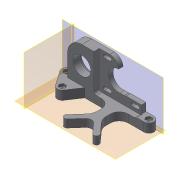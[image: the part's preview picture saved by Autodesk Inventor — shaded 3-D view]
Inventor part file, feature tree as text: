
AUTODESK INVENTOR PART (.ipt)
format: ipt  version: 2015 SP2 (Build 190223200, 223)  size: 351,744 bytes
history: native  units: mm
features: extrude x10, sketch x10, projected_geometry x4, chamfer x2, fillet x2, pattern_linear x2, other x1
ambient origin geometry x8: Origin, YZ Plane, XZ Plane, XY Plane, X Axis, Y Axis, Z Axis, Center Point
bodies: Body1 (feature_tree)
feature tree (31):
  other  "Sólido1"
  extrude  "Extrusión1"  Depth=5.5mm
  extrude  "Extrusión2"  Depth=5.0mm
  extrude  "Extrusión3"  Depth=10.0mm
  extrude  "Extrusión4"  Depth=3.0mm
  extrude  "Extrusión5"  Depth=6.0mm
  chamfer  "Chaflán2"  Distance=91.459mm
  chamfer  "Chaflán3"  Distance=5.5mm
  extrude  "Extrusión6"  Depth=11.967723mm
  extrude  "Extrusión7"  Depth=10.0mm
  extrude  "Extrusión8"  Depth=10.0mm
  fillet  "Empalme2"  Radius=3.76mm
  extrude  "Extrusión10"  Depth=10.0mm TaperAngle=0.0deg
  pattern_linear  "Patrón rectangular1"  Spacing1=6.235mm  [1 undecoded]
  pattern_linear  "Patrón rectangular2"  Spacing1=6.235mm  [1 undecoded]
  fillet  "Empalme3"  Radius=6.235mm
  extrude  "Extrusión11"  Depth=2.79mm TaperAngle=0.0deg
  sketch  "Boceto2"  dims[d19=91.459mm d20=5.5mm]
  sketch  "Boceto4"  dims[d21=5.0mm d22=5.0mm]
  sketch  "Boceto5"  dims[d25=10.0mm d28=14.666002mm]
  projected_geometry  "Contorno proyectado1"
  sketch  "Boceto6"  dims[d29=15.75mm d31=3.0mm]
  sketch  "Boceto7"  dims[d32=3.0mm d34=6.0mm]
  sketch  "Boceto8"  dims[d35=3.76mm]
  projected_geometry  "Contorno proyectado2"
  sketch  "Boceto9"  dims[d36=3.76mm]
  sketch  "Boceto10"  dims[d37=10.0mm]
  projected_geometry  "Contorno proyectado3"
  sketch  "Boceto12"  dims[d38=5.5mm]
  projected_geometry  "Contorno proyectado4"
  sketch  "Boceto13"  dims[d39=5.5mm d40=91.459mm d41=5.5mm d42=11.967723mm d43=21.587978mm d44=20.112mm d46=3.76mm d47=10.0mm d48=0.0mm d49=6.235mm d50=6.235mm d51=6.235mm d52=2.79mm d53=0.0mm d54=76.46mm d55=11.0mm d56=6.247mm d57=40.0mm d58=0.0mm d59=20.0mm d60=6.0mm d61=9.5mm d62=36.5mm d63=0.0mm d64=22.6mm d65=3.0mm d66=0.0mm d70=0.5mm d71=2.0mm d72=45.0deg d73=0.8mm d74=2.0mm d75=30.0deg d77=1.5mm d78=3.0mm d79=1.15mm d80=48.5mm d82=40.975mm d83=6.0mm d84=0.0mm d85=6.0mm d86=0.0mm d87=22.3mm d88=7.0mm d90=17.245mm d91=0.5mm d92=6.0mm d93=0.0mm d94=4.0mm d98=3.8mm d99=6.0mm d101=6.0mm d102=0.0mm d103=20.0mm d105=31.0mm d106=20.0mm d108=31.0mm d109=25.5mm d111=6.0mm d112=5.65mm d113=16.0mm d114=10.0mm d115=10.0mm d116=0.0mm]
note: 2 required parameter values undecoded (feature->parameter linkage not recoverable at this tier; creation-order binding heuristic only, values carry confidence <= 0.55)
